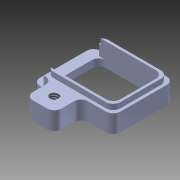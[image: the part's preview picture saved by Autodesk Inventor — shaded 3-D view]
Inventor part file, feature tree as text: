
AUTODESK INVENTOR PART (.ipt)
format: ipt  version: 2011 (Build 150239000, 239)  size: 160,256 bytes
history: native  units: in
note: dims shown in document units (in); Inventor stores cm internally (conversion verified against a paired STEP export)
features: other x1, imported_body x1, thread x1
ambient origin geometry x8: Origin, YZ Plane, XZ Plane, XY Plane, X Axis, Y Axis, Z Axis, Center Point
feature tree (3):
  other  "rectangle_window_D"
  imported_body  "Base1"
  thread  "Thread1"  [1 undecoded]
note: 1 required parameter value undecoded (feature->parameter linkage not recoverable at this tier; creation-order binding heuristic only, values carry confidence <= 0.55)
